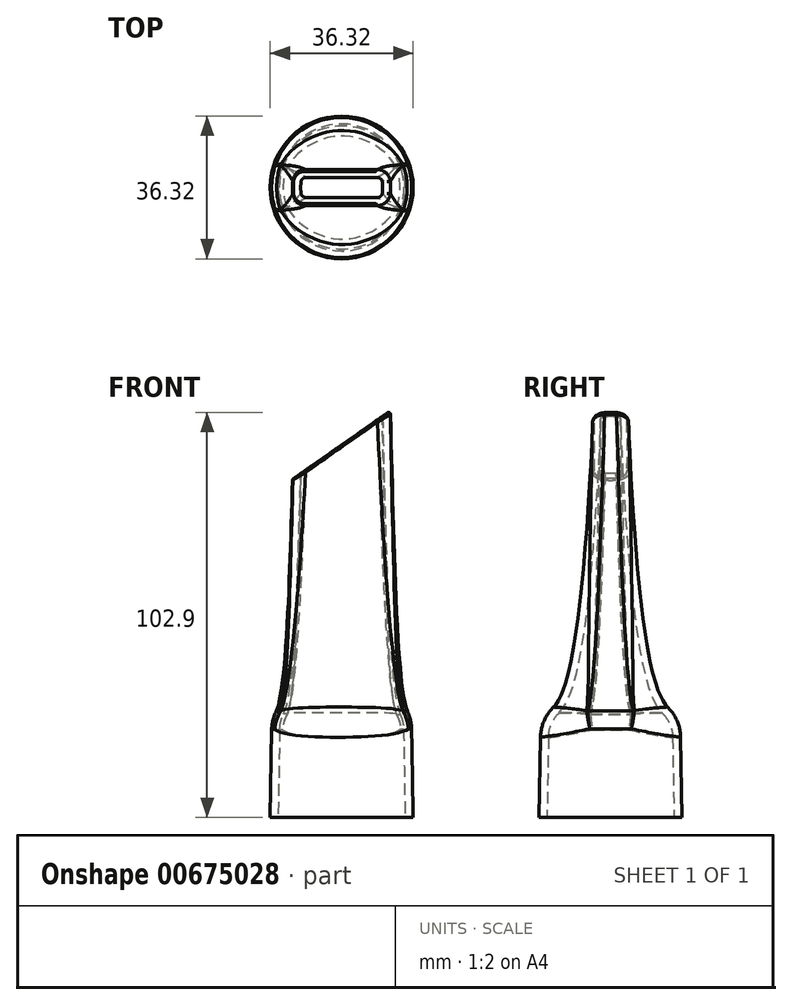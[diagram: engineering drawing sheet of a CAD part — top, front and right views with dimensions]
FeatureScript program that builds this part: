
annotation { "Feature Type Name" : "Feature", "Feature Type Description" : "" }
export const myFeature = defineFeature(function(context is Context, id is Id, definition is map)
    precondition{}
    {
        {
            var Q0;
            Q0=qCreatedBy(makeId("Top.planeOp"),FACE);
            var sketch = newSketch(context, id + "F0", { "sketchPlane" : qUnion([Q0])});
            skCircle(sketch, "E0", {"center": v(0, 0) * mm, "radius": 16.13 * mm});
            skSolve(sketch);
        }
        {
            var Q0;
            Q0=makeQuery(id+"F0.imprint","IMPRINT",FACE,{"disambiguationData":[TD([[makeQuery(id+"F0.imprint","IMPRINT",EDGE,{"derivedFrom":sQuery(id+"F0.wireOp",EDGE,"E0")}),1.0]])]});
            var Q1;
            Q1=sQuery(id+"F0.wireOp",EDGE,"E0");
            extrude(context, id + "F1", {"entities" : qUnion([Q0]), "surfaceEntities" : qUnion([Q1]), "depth" : 25.4 * mm, "offsetDistance" : 25.4 * mm, "hasDraft" : true, "draftAngle" : 1 * degree, "draftPullDirection" : true});
        }
        {
            var Q0;
            Q0=qCreatedBy(makeId("Front.planeOp"),FACE);
            var sketch = newSketch(context, id + "F2", { "sketchPlane" : qUnion([Q0])});
            skLineSegment(sketch, "E1", {"start": v(-98.93, 25.4) * mm, "end": v(28.09, 114.34) * mm, "construction": true});
            skLineSegment(sketch, "E2", {"start": v(0, 0) * mm, "end": v(-98.93, 0) * mm, "construction": true});
            skLineSegment(sketch, "E3", {"start": v(-98.93, 0) * mm, "end": v(-98.93, 25.4) * mm});
            skSolve(sketch);
        }
        {
            var Q0;
            Q0=sQuery(id+"F2.wireOp",EDGE,"E1");
            cPlane(context, id + "F3", {"entities" : qUnion([Q0]), "cplaneType" : CPlaneType.LINE_ANGLE, "offset" : 25.4 * mm, "angle" : 90 * degree, "width" : 152.4 * mm, "height" : 152.4 * mm});
        }
        {
            var Q0;
            Q0=qCreatedBy(id+"F3.planeOp",FACE);
            var sketch = newSketch(context, id + "F4", { "sketchPlane" : qUnion([Q0])});
            skLineSegment(sketch, "E4.left", {"start": v(66.74, 2.54) * mm, "end": v(41.86, 2.54) * mm});
            skLineSegment(sketch, "E4.right", {"start": v(66.74, -2.54) * mm, "end": v(41.86, -2.54) * mm});
            skLineSegment(sketch, "E5", {"start": v(41.6, 0) * mm, "end": v(67, 0) * mm, "construction": true});
            skLineSegment(sketch, "E6", {"start": v(54.3, 75.68) * mm, "end": v(54.3, -57.36) * mm, "construction": true});
            skArc(sketch, "E7", {"start": v(66.74, -2.54) * mm, "mid": v(67, 0) * mm, "end": v(66.74, 2.54) * mm});
            skArc(sketch, "E8", {"start": v(41.86, 2.54) * mm, "mid": v(41.6, 0) * mm, "end": v(41.86, -2.54) * mm});
            skSolve(sketch);
        }
        {
            var Q0;
            Q0=makeQuery(id+"F1.opExtrude","CAP_FACE",FACE,{"disambiguationData":[OSD([sQuery(id+"F0.wireOp",EDGE,"E0")])],"isStart":false});
            var sketch = newSketch(context, id + "F5", { "sketchPlane" : qUnion([Q0])});
            skArc(sketch, "E9", {"start": v(-14.6, 5.72) * mm, "mid": v(-15.69, 0) * mm, "end": v(-14.6, -5.72) * mm});
            skArc(sketch, "E10", {"start": v(-14.6, -5.72) * mm, "mid": v(0, -15.69) * mm, "end": v(14.6, -5.72) * mm});
            skArc(sketch, "E11", {"start": v(14.6, -5.72) * mm, "mid": v(15.69, 0) * mm, "end": v(14.6, 5.72) * mm});
            skArc(sketch, "E12", {"start": v(14.6, 5.72) * mm, "mid": v(0, 15.69) * mm, "end": v(-14.6, 5.72) * mm});
            skLineSegment(sketch, "E13", {"start": v(-14.6, 5.72) * mm, "end": v(-14.6, -5.72) * mm, "construction": true});
            skLineSegment(sketch, "E14", {"start": v(14.6, 5.72) * mm, "end": v(14.6, -5.72) * mm, "construction": true});
            skLineSegment(sketch, "E15", {"start": v(-14.6, 0) * mm, "end": v(14.6, 0) * mm, "construction": true});
            skSolve(sketch);
        }
        {
            var Q1;
            Q1 = qSketchRegion(id + "F5", true);
            var Q2;
            Q2=makeQuery(id+"F4.imprint","IMPRINT",FACE,{"disambiguationData":[TD([[makeQuery(id+"F4.imprint","IMPRINT",EDGE,{"derivedFrom":sQuery(id+"F4.wireOp",EDGE,"E4.left")}),1.0]])]});
            loft(context, id + "F6", {"operationType" : NewBodyOperationType.ADD, "startCondition" : LoftEndDerivativeType.TANGENT_TO_PROFILE, "startMagnitude" : 2, "sheetProfilesArray" : [{ "sheetProfileEntities" : qUnion([Q1]) }, { "sheetProfileEntities" : qUnion([Q2]) }]});
        }
        {
            var Q0;
            Q0=makeQuery(id+"F6.boolean.opBoolean","MERGE",EDGE,{"derivedFrom":[makeQuery(id+"F1.opExtrude","CAP_EDGE",EDGE,{"disambiguationData":[OSD([sQuery(id+"F0.wireOp",EDGE,"E0")])],"isStart":false}),makeQuery(id+"F6.opLoft","MID_CAP_EDGE",EDGE,{"disambiguationData":[OSD([sQuery(id+"F5.wireOp",EDGE,"E9"),sQuery(id+"F5.wireOp",EDGE,"E10"),sQuery(id+"F5.wireOp",EDGE,"E11")])],"capPos":0.0})]});
            var Q1;
            Q1=makeQuery(id+"F6.boolean.opBoolean","MERGE",EDGE,{"derivedFrom":[makeQuery(id+"F1.opExtrude","CAP_EDGE",EDGE,{"disambiguationData":[OSD([sQuery(id+"F0.wireOp",EDGE,"E0")])],"isStart":false}),makeQuery(id+"F6.opLoft","MID_CAP_EDGE",EDGE,{"disambiguationData":[OSD([sQuery(id+"F5.wireOp",EDGE,"E9"),sQuery(id+"F5.wireOp",EDGE,"E10"),sQuery(id+"F5.wireOp",EDGE,"E12")])],"capPos":0.0})]});
            var Q2;
            Q2=makeQuery(id+"F6.boolean.opBoolean","MERGE",EDGE,{"derivedFrom":[makeQuery(id+"F1.opExtrude","CAP_EDGE",EDGE,{"disambiguationData":[OSD([sQuery(id+"F0.wireOp",EDGE,"E0")])],"isStart":false}),makeQuery(id+"F6.opLoft","MID_CAP_EDGE",EDGE,{"disambiguationData":[OSD([sQuery(id+"F5.wireOp",EDGE,"E9"),sQuery(id+"F5.wireOp",EDGE,"E11"),sQuery(id+"F5.wireOp",EDGE,"E12")])],"capPos":0.0})]});
            var Q3;
            Q3=makeQuery(id+"F6.boolean.opBoolean","MERGE",EDGE,{"derivedFrom":[makeQuery(id+"F1.opExtrude","CAP_EDGE",EDGE,{"disambiguationData":[OSD([sQuery(id+"F0.wireOp",EDGE,"E0")])],"isStart":false}),makeQuery(id+"F6.opLoft","MID_CAP_EDGE",EDGE,{"disambiguationData":[OSD([sQuery(id+"F5.wireOp",EDGE,"E10"),sQuery(id+"F5.wireOp",EDGE,"E11"),sQuery(id+"F5.wireOp",EDGE,"E12")])],"capPos":0.0})]});
            fillet(context, id + "F7", {"entities" : qUnion([Q0, Q1, Q2, Q3]), "radius" : 8.9 * mm, "tangentPropagation" : true, "allowEdgeOverflow" : false});
        }
        {
            var Q0;
            Q0=makeQuery(id+"F6.opLoft","SWEPT_EDGE",EDGE,{"disambiguationData":[OSD([sQuery(id+"F4.wireOp",EDGE,"E4.right"),sQuery(id+"F4.wireOp",EDGE,"E7"),sQuery(id+"F5.wireOp",EDGE,"E10"),sQuery(id+"F5.wireOp",EDGE,"E11")])]});
            var Q1;
            Q1=makeQuery(id+"F6.opLoft","SWEPT_EDGE",EDGE,{"disambiguationData":[OSD([sQuery(id+"F4.wireOp",EDGE,"E4.left"),sQuery(id+"F4.wireOp",EDGE,"E7"),sQuery(id+"F5.wireOp",EDGE,"E11"),sQuery(id+"F5.wireOp",EDGE,"E12")])]});
            var Q2;
            Q2=makeQuery(id+"F6.opLoft","SWEPT_EDGE",EDGE,{"disambiguationData":[OSD([sQuery(id+"F4.wireOp",EDGE,"E4.right"),sQuery(id+"F4.wireOp",EDGE,"E8"),sQuery(id+"F5.wireOp",EDGE,"E9"),sQuery(id+"F5.wireOp",EDGE,"E10")])]});
            var Q3;
            Q3=makeQuery(id+"F6.opLoft","SWEPT_EDGE",EDGE,{"disambiguationData":[OSD([sQuery(id+"F4.wireOp",EDGE,"E4.left"),sQuery(id+"F4.wireOp",EDGE,"E8"),sQuery(id+"F5.wireOp",EDGE,"E9"),sQuery(id+"F5.wireOp",EDGE,"E12")])]});
            fillet(context, id + "F8", {"entities" : qUnion([Q0, Q1, Q2, Q3]), "radius" : 1.27 * mm, "tangentPropagation" : true, "allowEdgeOverflow" : false});
        }
        {
            var Q0;
            Q0=makeQuery(id+"F6.opLoft","CAP_FACE",FACE,{"disambiguationData":[OSD([makeQuery(id+"F4.imprint","IMPRINT",FACE,{"disambiguationData":[TD([[makeQuery(id+"F4.imprint","IMPRINT",EDGE,{"derivedFrom":sQuery(id+"F4.wireOp",EDGE,"E4.left")}),1.0]])]})])],"isStart":true});
            var Q1;
            Q1=makeQuery(id+"F1.opExtrude","CAP_FACE",FACE,{"disambiguationData":[OSD([sQuery(id+"F0.wireOp",EDGE,"E0")])],"isStart":true});
            shell(context, id + "F9", {"entities" : qUnion([Q0, Q1]), "thickness" : 2.03 * mm, "oppositeDirection" : true});
        }
        {
            var Q0;
            Q0=makeQuery(id+"F6.opLoft","MID_CAP_EDGE",EDGE,{"disambiguationData":[OSD([sQuery(id+"F4.wireOp",EDGE,"E4.right"),sQuery(id+"F4.wireOp",EDGE,"E7"),sQuery(id+"F4.wireOp",EDGE,"E8")])],"capPos":1.0});
            fillet(context, id + "F10", {"entities" : qUnion([Q0]), "radius" : 0.5 * mm, "tangentPropagation" : true, "allowEdgeOverflow" : false});
        }
    });
